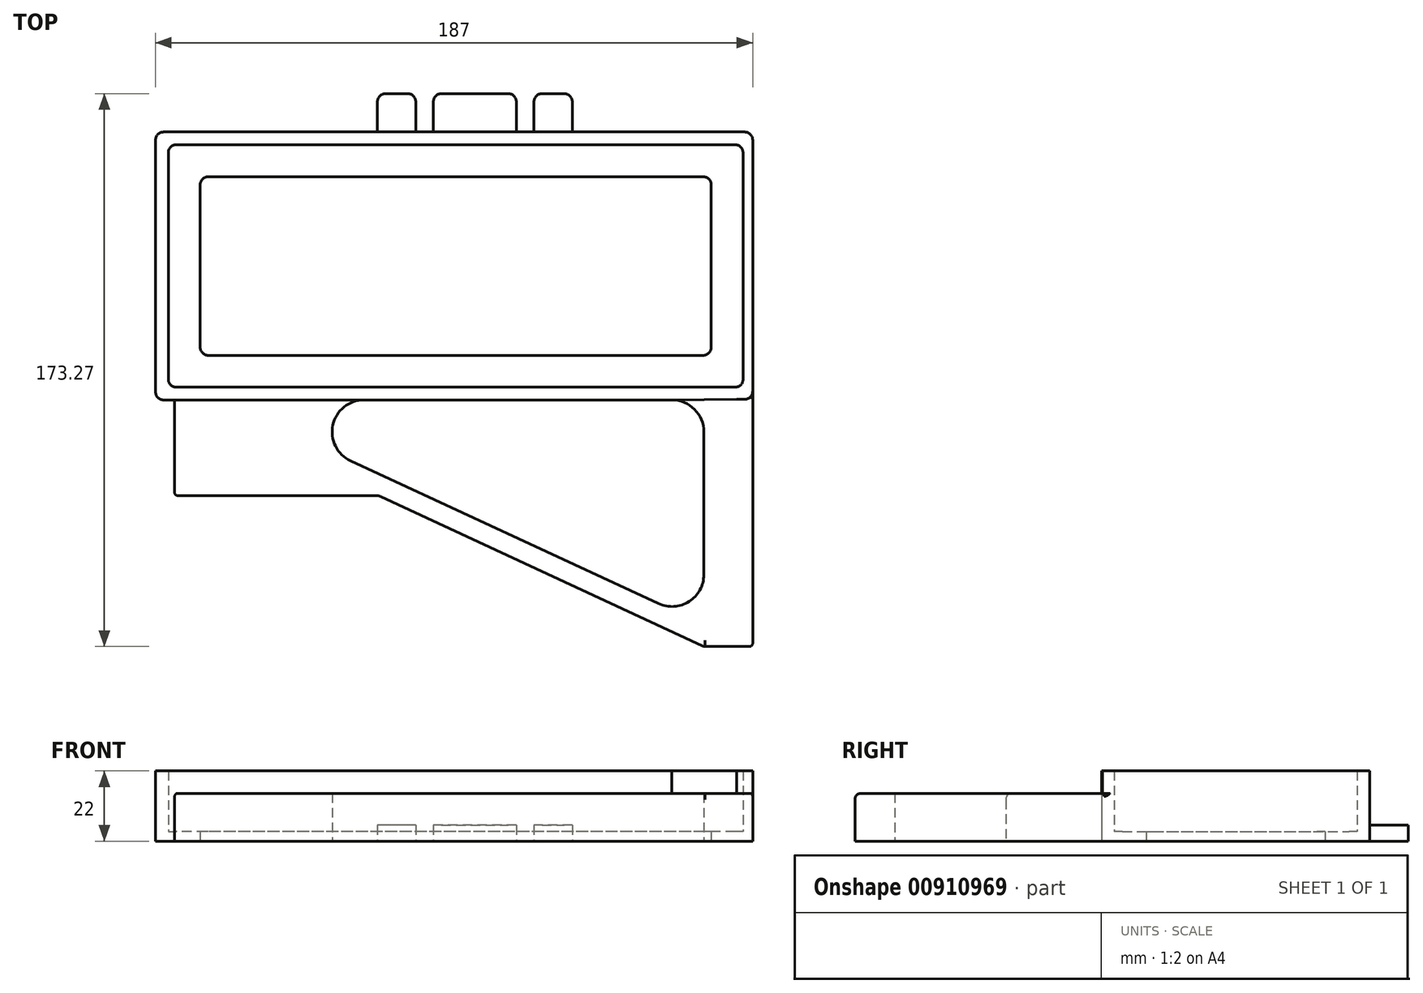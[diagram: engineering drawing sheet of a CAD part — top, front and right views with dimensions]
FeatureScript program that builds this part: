
annotation { "Feature Type Name" : "Feature", "Feature Type Description" : "" }
export const myFeature = defineFeature(function(context is Context, id is Id, definition is map)
    precondition{}
    {
        {
            var Q0;
            Q0=qCreatedBy(makeId("Top.planeOp"),FACE);
            var sketch = newSketch(context, id + "F0", { "sketchPlane" : qUnion([Q0])});
            skLineSegment(sketch, "E0.bottom", {"start": v(87.5, 0) * mm, "end": v(-87.5, 0) * mm});
            skLineSegment(sketch, "E0.top", {"start": v(87.5, 76) * mm, "end": v(-87.5, 76) * mm});
            skLineSegment(sketch, "E0.left", {"start": v(90, 2.5) * mm, "end": v(90, 73.5) * mm});
            skLineSegment(sketch, "E0.right", {"start": v(-90, 2.5) * mm, "end": v(-90, 73.5) * mm});
            skLineSegment(sketch, "E1.0", {"start": v(102, 80) * mm, "end": v(-74, 80) * mm});
            skLineSegment(sketch, "E2.0", {"start": v(-94, 0) * mm, "end": v(-94, 76) * mm});
            skLineSegment(sketch, "E3.0", {"start": v(67.7, -4) * mm, "end": v(-28.7, -4) * mm});
            skLineSegment(sketch, "E4.0", {"start": v(93, 0) * mm, "end": v(93, 76) * mm});
            skLineSegment(sketch, "E5", {"start": v(-74, 80) * mm, "end": v(-91.5, 80) * mm});
            skLineSegment(sketch, "E6", {"start": v(-94, 76) * mm, "end": v(-94, 77.5) * mm});
            skLineSegment(sketch, "E7", {"start": v(-94, -1.5) * mm, "end": v(-94, 0) * mm});
            skLineSegment(sketch, "E8", {"start": v(-88, -4) * mm, "end": v(-91.5, -4) * mm});
            skLineSegment(sketch, "E9", {"start": v(90.5, 80) * mm, "end": v(102, 80) * mm});
            skLineSegment(sketch, "E10", {"start": v(93, 77.5) * mm, "end": v(93, 76) * mm});
            skLineSegment(sketch, "E11", {"start": v(88, -3.77) * mm, "end": v(90.5, -3.77) * mm});
            skLineSegment(sketch, "E12", {"start": v(93, -1.27) * mm, "end": v(93, 0) * mm});
            skLineSegment(sketch, "E13", {"start": v(-7, 80) * mm, "end": v(-7, 89.5) * mm});
            skLineSegment(sketch, "E14", {"start": v(-4.5, 92) * mm, "end": v(16.5, 92) * mm});
            skLineSegment(sketch, "E15", {"start": v(19, 89.5) * mm, "end": v(19, 80) * mm});
            skLineSegment(sketch, "E16", {"start": v(6, 92) * mm, "end": v(6, 80) * mm, "construction": true});
            skLineSegment(sketch, "E17", {"start": v(6, 80) * mm, "end": v(6, 76) * mm, "construction": true});
            skLineSegment(sketch, "E18", {"start": v(-12.5, 80) * mm, "end": v(-12.5, 89.5) * mm});
            skLineSegment(sketch, "E19", {"start": v(-15, 92) * mm, "end": v(-22, 92) * mm});
            skLineSegment(sketch, "E20", {"start": v(-24.5, 89.5) * mm, "end": v(-24.5, 80) * mm});
            skLineSegment(sketch, "E21", {"start": v(24.5, 80) * mm, "end": v(24.5, 89.5) * mm});
            skLineSegment(sketch, "E22", {"start": v(27, 92) * mm, "end": v(34, 92) * mm});
            skLineSegment(sketch, "E23", {"start": v(36.5, 89.5) * mm, "end": v(36.5, 80) * mm});
            skPoint(sketch, "E24.visualSharp", {"position": v(19, 92) * mm});
            skArc(sketch, "E24.filletArc", {"start": v(19, 89.5) * mm, "mid": v(18.27, 91.27) * mm, "end": v(16.5, 92) * mm});
            skPoint(sketch, "E25.visualSharp", {"position": v(-7, 92) * mm});
            skArc(sketch, "E25.filletArc", {"start": v(-4.5, 92) * mm, "mid": v(-6.27, 91.27) * mm, "end": v(-7, 89.5) * mm});
            skPoint(sketch, "E26.visualSharp", {"position": v(-12.5, 92) * mm});
            skArc(sketch, "E26.filletArc", {"start": v(-12.5, 89.5) * mm, "mid": v(-13.23, 91.27) * mm, "end": v(-15, 92) * mm});
            skPoint(sketch, "E27.visualSharp", {"position": v(24.5, 92) * mm});
            skArc(sketch, "E27.filletArc", {"start": v(27, 92) * mm, "mid": v(25.23, 91.27) * mm, "end": v(24.5, 89.5) * mm});
            skPoint(sketch, "E28.visualSharp", {"position": v(-24.5, 92) * mm});
            skArc(sketch, "E28.filletArc", {"start": v(-22, 92) * mm, "mid": v(-23.77, 91.27) * mm, "end": v(-24.5, 89.5) * mm});
            skPoint(sketch, "E29.visualSharp", {"position": v(36.5, 92) * mm});
            skArc(sketch, "E29.filletArc", {"start": v(36.5, 89.5) * mm, "mid": v(35.77, 91.27) * mm, "end": v(34, 92) * mm});
            skPoint(sketch, "E30.visualSharp", {"position": v(-90, 76) * mm});
            skArc(sketch, "E30.filletArc", {"start": v(-87.5, 76) * mm, "mid": v(-89.27, 75.27) * mm, "end": v(-90, 73.5) * mm});
            skPoint(sketch, "E31.visualSharp", {"position": v(-94, 80) * mm});
            skArc(sketch, "E31.filletArc", {"start": v(-91.5, 80) * mm, "mid": v(-93.27, 79.27) * mm, "end": v(-94, 77.5) * mm});
            skPoint(sketch, "E32.visualSharp", {"position": v(-90, 0) * mm});
            skArc(sketch, "E32.filletArc", {"start": v(-90, 2.5) * mm, "mid": v(-89.27, 0.73) * mm, "end": v(-87.5, 0) * mm});
            skPoint(sketch, "E33.visualSharp", {"position": v(-94, -4) * mm});
            skArc(sketch, "E33.filletArc", {"start": v(-94, -1.5) * mm, "mid": v(-93.27, -3.27) * mm, "end": v(-91.5, -4) * mm});
            skPoint(sketch, "E34.visualSharp", {"position": v(93, -3.77) * mm});
            skArc(sketch, "E34.filletArc", {"start": v(90.5, -3.77) * mm, "mid": v(92.27, -3.03) * mm, "end": v(93, -1.27) * mm});
            skPoint(sketch, "E35.visualSharp", {"position": v(90, 0) * mm});
            skArc(sketch, "E35.filletArc", {"start": v(87.5, 0) * mm, "mid": v(89.27, 0.73) * mm, "end": v(90, 2.5) * mm});
            skPoint(sketch, "E36.visualSharp", {"position": v(90, 76) * mm});
            skArc(sketch, "E36.filletArc", {"start": v(90, 73.5) * mm, "mid": v(89.27, 75.27) * mm, "end": v(87.5, 76) * mm});
            skPoint(sketch, "E37.visualSharp", {"position": v(93, 80) * mm});
            skArc(sketch, "E37.filletArc", {"start": v(93, 77.5) * mm, "mid": v(92.27, 79.27) * mm, "end": v(90.5, 80) * mm});
            skLineSegment(sketch, "E38.0", {"start": v(77.5, 66) * mm, "end": v(-77.5, 66) * mm});
            skLineSegment(sketch, "E39.0", {"start": v(80, 12.5) * mm, "end": v(80, 63.5) * mm});
            skLineSegment(sketch, "E40.0", {"start": v(77.5, 10) * mm, "end": v(-77.5, 10) * mm});
            skLineSegment(sketch, "E41.0", {"start": v(-80, 12.5) * mm, "end": v(-80, 63.5) * mm});
            skPoint(sketch, "E42.visualSharp", {"position": v(-80, 66) * mm});
            skArc(sketch, "E42.filletArc", {"start": v(-77.5, 66) * mm, "mid": v(-79.27, 65.27) * mm, "end": v(-80, 63.5) * mm});
            skPoint(sketch, "E43.visualSharp", {"position": v(-80, 10) * mm});
            skArc(sketch, "E43.filletArc", {"start": v(-80, 12.5) * mm, "mid": v(-79.27, 10.73) * mm, "end": v(-77.5, 10) * mm});
            skPoint(sketch, "E44.visualSharp", {"position": v(80, 66) * mm});
            skArc(sketch, "E44.filletArc", {"start": v(80, 63.5) * mm, "mid": v(79.27, 65.27) * mm, "end": v(77.5, 66) * mm});
            skPoint(sketch, "E45.visualSharp", {"position": v(80, 10) * mm});
            skArc(sketch, "E45.filletArc", {"start": v(77.5, 10) * mm, "mid": v(79.27, 10.73) * mm, "end": v(80, 12.5) * mm});
            skLineSegment(sketch, "E46", {"start": v(93, -1.27) * mm, "end": v(93, -81.27) * mm});
            skLineSegment(sketch, "E47", {"start": v(93, -81.27) * mm, "end": v(77.65, -81.27) * mm});
            skLineSegment(sketch, "E48", {"start": v(-88, -4) * mm, "end": v(-88, -34) * mm});
            skLineSegment(sketch, "E49", {"start": v(-88, -34) * mm, "end": v(-73, -34) * mm});
            skLineSegment(sketch, "E50", {"start": v(-73, -34) * mm, "end": v(-73, -4) * mm});
            skLineSegment(sketch, "E51", {"start": v(-23.52, -34.23) * mm, "end": v(77.65, -81.27) * mm});
            skLineSegment(sketch, "E52", {"start": v(63.5, -67.8) * mm, "end": v(-32.9, -23.07) * mm});
            skArc(sketch, "E53.filletArc", {"start": v(77.7, -14) * mm, "mid": v(74.78, -6.93) * mm, "end": v(67.7, -4) * mm});
            skLineSegment(sketch, "E54", {"start": v(67.7, -4) * mm, "end": v(88, -3.77) * mm});
            skLineSegment(sketch, "E55", {"start": v(77.7, -14) * mm, "end": v(77.7, -58.74) * mm});
            skLineSegment(sketch, "E56", {"start": v(77.65, -74.17) * mm, "end": v(77.65, -81.27) * mm});
            skArc(sketch, "E57.filletArc", {"start": v(63.5, -67.8) * mm, "mid": v(73.09, -67.17) * mm, "end": v(77.7, -58.74) * mm});
            skPoint(sketch, "E58.newPointA", {"position": v(-88, -4) * mm});
            skArc(sketch, "E58.filletArc", {"start": v(-28.7, -4) * mm, "mid": v(-38.46, -11.84) * mm, "end": v(-32.9, -23.07) * mm});
            skLineSegment(sketch, "E59", {"start": v(-28.7, -4) * mm, "end": v(-88, -4) * mm});
            skLineSegment(sketch, "E60", {"start": v(6, 76) * mm, "end": v(6, -4) * mm, "construction": true});
            skLineSegment(sketch, "E61", {"start": v(-73, -34) * mm, "end": v(-24.57, -34) * mm});
            skArc(sketch, "E62.filletArc", {"start": v(-23.52, -34.23) * mm, "mid": v(-24.03, -34.06) * mm, "end": v(-24.57, -34) * mm});
            skSolve(sketch);
        }
        {
            var Q0;
            Q0=makeQuery(id+"F0.imprint","IMPRINT",FACE,{"disambiguationData":[TD([[makeQuery(id+"F0.imprint","IMPRINT",EDGE,{"derivedFrom":sQuery(id+"F0.wireOp",EDGE,"E0.bottom")}),1.0]])]});
            extrude(context, id + "F1", {"entities" : qUnion([Q0]), "depth" : 22 * mm, "offsetDistance" : 25 * mm});
        }
        {
            var Q0;
            Q0=makeQuery(id+"F0.imprint","IMPRINT",FACE,{"disambiguationData":[TD([[makeQuery(id+"F0.imprint","IMPRINT",EDGE,{"derivedFrom":sQuery(id+"F0.wireOp",EDGE,"E0.bottom")}),-1.0]])]});
            extrude(context, id + "F2", {"entities" : qUnion([Q0]), "operationType" : NewBodyOperationType.ADD, "depth" : 3 * mm, "offsetDistance" : 25 * mm});
        }
        {
            var Q0;
            {var subQ0=sQuery(id+"F0.wireOp",EDGE,"E11");Q0=makeQuery(id+"F0.imprint","IMPRINT",FACE,{"disambiguationData":[TD([[makeQuery(id+"F0.imprint","IMPRINT",EDGE,{"derivedFrom":subQ0}),-1.0]])]});}
            var Q1;
            {var subQ0=sQuery(id+"F0.wireOp",EDGE,"E47");Q1=makeQuery(id+"F0.imprint","IMPRINT",FACE,{"disambiguationData":[TD([[makeQuery(id+"F0.imprint","IMPRINT",EDGE,{"derivedFrom":subQ0}),-1.0]])]});}
            extrude(context, id + "F3", {"entities" : qUnion([Q0, Q1]), "operationType" : NewBodyOperationType.ADD, "depth" : 15 * mm, "offsetDistance" : 25 * mm});
        }
        {
            var Q0;
            {var subQ1=sQuery(id+"F0.wireOp",EDGE,"Ny0Gnn2i-Ygqb-VPq2-N1I1-QU3OLZ8xniGR");var subQ3=sQuery(id+"F0.wireOp",EDGE,"E52");var subQ4=makeQuery(id+"F0.imprint","INTERSECT",VERTEX,{"derivedFrom":[subQ1,subQ3]});Q0=makeQuery(id+"F0.imprint","IMPRINT",FACE,{"disambiguationData":[TD([[makeQuery(id+"F0.imprint","IMPRINT",EDGE,{"disambiguationData":[TD([[subQ4,1.0]])],"derivedFrom":subQ1}),1.0]])]});}
            var Q1;
            {var subQ0=sQuery(id+"F0.wireOp",EDGE,"E59");var subQ5=sQuery(id+"F0.wireOp",EDGE,"E50");var subQ6=makeQuery(id+"F0.imprint","INTERSECT",VERTEX,{"derivedFrom":[subQ5,subQ0]});Q1=makeQuery(id+"F0.imprint","IMPRINT",FACE,{"disambiguationData":[TD([[makeQuery(id+"F0.imprint","IMPRINT",EDGE,{"disambiguationData":[TD([[subQ6,1.0]])],"derivedFrom":subQ5}),1.0]])]});}
            var Q2;
            {var subQ0=sQuery(id+"F0.wireOp",EDGE,"fGbPgxKb-3OdY-1Y91-8G2S-CM4cBlenFRyz");Q2=makeQuery(id+"F0.imprint","IMPRINT",FACE,{"disambiguationData":[TD([[makeQuery(id+"F0.imprint","IMPRINT",EDGE,{"derivedFrom":subQ0}),1.0]])]});}
            var Q3;
            {var subQ0=sQuery(id+"F0.wireOp",EDGE,"E48");Q3=makeQuery(id+"F0.imprint","IMPRINT",FACE,{"disambiguationData":[TD([[makeQuery(id+"F0.imprint","IMPRINT",EDGE,{"derivedFrom":subQ0}),1.0]])]});}
            extrude(context, id + "F4", {"entities" : qUnion([Q0, Q1, Q2, Q3]), "operationType" : NewBodyOperationType.ADD, "depth" : 15 * mm, "offsetDistance" : 25 * mm});
        }
        {
            var Q0;
            Q0=makeQuery(id+"F3.opExtrude","CAP_EDGE",EDGE,{"disambiguationData":[OSD([sQuery(id+"F0.wireOp",EDGE,"E47")])],"isStart":false});
            fillet(context, id + "F5", {"entities" : qUnion([Q0]), "radius" : 2 * mm, "tangentPropagation" : true, "allowEdgeOverflow" : false});
        }
        {
            var Q0;
            Q0=makeQuery(id+"F3.opExtrude","CAP_EDGE",EDGE,{"disambiguationData":[OSD([sQuery(id+"F0.wireOp",EDGE,"E51")])],"isStart":false});
            fillet(context, id + "F6", {"entities" : qUnion([Q0]), "radius" : 2 * mm, "tangentPropagation" : true, "allowEdgeOverflow" : false});
        }
        {
            var Q0;
            Q0=makeQuery(id+"F3.opExtrude","SWEPT_EDGE",EDGE,{"disambiguationData":[OSD([sQuery(id+"F0.wireOp",EDGE,"E46"),sQuery(id+"F0.wireOp",EDGE,"E47")])]});
            fillet(context, id + "F7", {"entities" : qUnion([Q0]), "radius" : 1 * mm, "tangentPropagation" : true, "allowEdgeOverflow" : false});
        }
        {
            var Q0;
            Q0=makeQuery(id+"F4.opExtrude","SWEPT_EDGE",EDGE,{"disambiguationData":[OSD([sQuery(id+"F0.wireOp",EDGE,"E48"),sQuery(id+"F0.wireOp",EDGE,"E49")])]});
            fillet(context, id + "F8", {"entities" : qUnion([Q0]), "radius" : 1 * mm, "tangentPropagation" : true, "allowEdgeOverflow" : false});
        }
        {
            var Q0;
            {var subQ1=sQuery(id+"F0.wireOp",EDGE,"E18");Q0=makeQuery(id+"F0.imprint","IMPRINT",FACE,{"disambiguationData":[TD([[makeQuery(id+"F0.imprint","IMPRINT",EDGE,{"derivedFrom":subQ1}),1.0]])]});}
            var Q1;
            {var subQ1=sQuery(id+"F0.wireOp",EDGE,"E13");Q1=makeQuery(id+"F0.imprint","IMPRINT",FACE,{"disambiguationData":[TD([[makeQuery(id+"F0.imprint","IMPRINT",EDGE,{"derivedFrom":subQ1}),-1.0]])]});}
            var Q2;
            {var subQ1=sQuery(id+"F0.wireOp",EDGE,"E21");Q2=makeQuery(id+"F0.imprint","IMPRINT",FACE,{"disambiguationData":[TD([[makeQuery(id+"F0.imprint","IMPRINT",EDGE,{"derivedFrom":subQ1}),-1.0]])]});}
            extrude(context, id + "F9", {"entities" : qUnion([Q0, Q1, Q2]), "operationType" : NewBodyOperationType.ADD, "depth" : 5 * mm, "offsetDistance" : 25 * mm});
        }
    });
